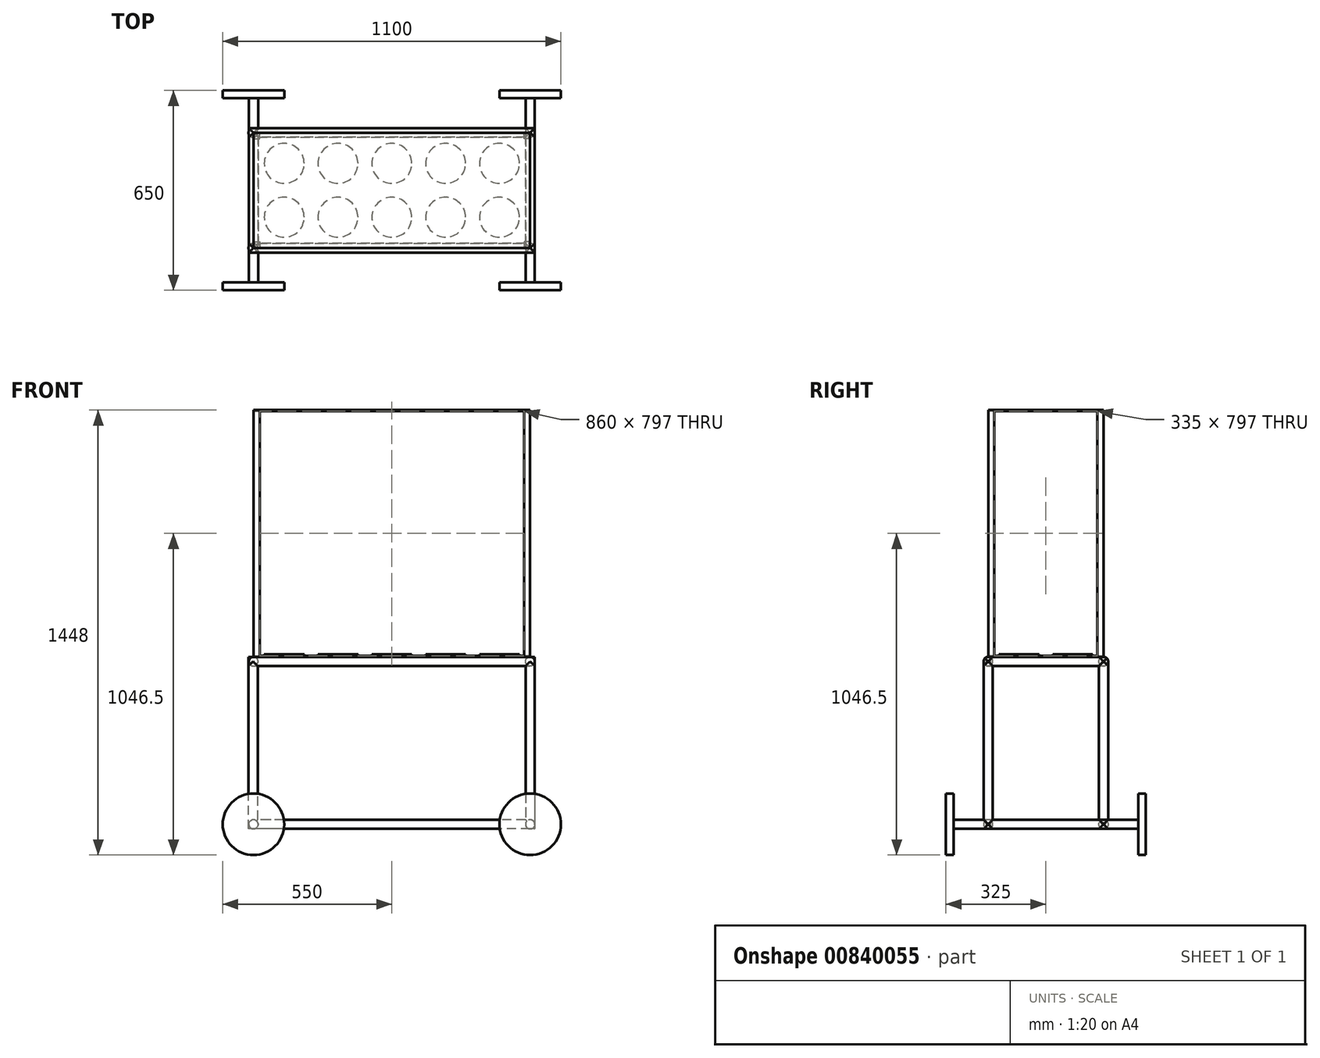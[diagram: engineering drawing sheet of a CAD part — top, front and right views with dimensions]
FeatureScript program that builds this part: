
annotation { "Feature Type Name" : "Feature", "Feature Type Description" : "" }
export const myFeature = defineFeature(function(context is Context, id is Id, definition is map)
    precondition{}
    {
        {
            var Q0;
            Q0=qCreatedBy(makeId("Top.planeOp"),FACE);
            var sketch = newSketch(context, id + "F0", { "sketchPlane" : qUnion([Q0])});
            skLineSegment(sketch, "E0", {"start": v(-450, 0) * mm, "end": v(-450, 187.5) * mm});
            skLineSegment(sketch, "E1", {"start": v(-450, 187.5) * mm, "end": v(0, 187.5) * mm});
            skLineSegment(sketch, "E2.MirrorCS", {"start": v(450, 0) * mm, "end": v(450, 187.5) * mm});
            skLineSegment(sketch, "E3.MirrorCS", {"start": v(450, 187.5) * mm, "end": v(0, 187.5) * mm});
            skLineSegment(sketch, "E4.MirrorCS", {"start": v(-450, 0) * mm, "end": v(-450, -187.5) * mm});
            skLineSegment(sketch, "E5.MirrorCS", {"start": v(-450, -187.5) * mm, "end": v(0, -187.5) * mm});
            skLineSegment(sketch, "E6.MirrorCS", {"start": v(450, -187.5) * mm, "end": v(0, -187.5) * mm});
            skLineSegment(sketch, "E7.MirrorCS", {"start": v(450, 0) * mm, "end": v(450, -187.5) * mm});
            skSolve(sketch);
        }
        {
            var Q0;
            Q0=qCreatedBy(makeId("Right.planeOp"),FACE);
            var sketch = newSketch(context, id + "F1", { "sketchPlane" : qUnion([Q0])});
            skCircle(sketch, "E8", {"center": v(187.5, 0) * mm, "radius": 15 * mm});
            skSolve(sketch);
        }
        {
            var Q0;
            Q0=makeQuery(id+"F0.imprint","IMPRINT",FACE,{"disambiguationData":[TD([[makeQuery(id+"F0.imprint","IMPRINT",EDGE,{"derivedFrom":sQuery(id+"F0.wireOp",EDGE,"E0")}),-1.0]])]});
            cPlane(context, id + "F2", {"entities" : qUnion([Q0]), "cplaneType" : CPlaneType.OFFSET, "offset" : 530 * mm, "width" : 150 * mm, "height" : 150 * mm});
        }
        {
            var Q0;
            Q0=qCreatedBy(id+"F2.planeOp",FACE);
            var sketch = newSketch(context, id + "F3", { "sketchPlane" : qUnion([Q0])});
            skLineSegment(sketch, "E9", {"start": v(-450, -187.5) * mm, "end": v(-450, 187.5) * mm});
            skLineSegment(sketch, "E10", {"start": v(-450, 187.5) * mm, "end": v(450, 187.5) * mm});
            skLineSegment(sketch, "E11", {"start": v(450, 187.5) * mm, "end": v(450, -187.5) * mm});
            skLineSegment(sketch, "E12", {"start": v(450, -187.5) * mm, "end": v(-450, -187.5) * mm});
            skSolve(sketch);
        }
        {
            var Q0;
            Q0=qCreatedBy(makeId("Front.planeOp"),FACE);
            cPlane(context, id + "F4", {"entities" : qUnion([Q0]), "cplaneType" : CPlaneType.OFFSET, "offset" : 187.5 * mm, "width" : 150 * mm, "height" : 150 * mm});
        }
        {
            var Q0;
            Q0=qCreatedBy(id+"F4.planeOp",FACE);
            var sketch = newSketch(context, id + "F5", { "sketchPlane" : qUnion([Q0])});
            skLineSegment(sketch, "E13", {"start": v(-450, 0) * mm, "end": v(-450, 530) * mm});
            skLineSegment(sketch, "E14", {"start": v(-450, 530) * mm, "end": v(450, 530) * mm});
            skLineSegment(sketch, "E15", {"start": v(450, 530) * mm, "end": v(450, 0) * mm});
            skLineSegment(sketch, "E16", {"start": v(450, 0) * mm, "end": v(-450, 0) * mm});
            skSolve(sketch);
        }
        {
            var Q0;
            Q0=qCreatedBy(makeId("Front.planeOp"),FACE);
            cPlane(context, id + "F6", {"entities" : qUnion([Q0]), "cplaneType" : CPlaneType.OFFSET, "offset" : 187.5 * mm, "oppositeDirection" : true, "width" : 150 * mm, "height" : 150 * mm});
        }
        {
            var Q0;
            Q0=qCreatedBy(id+"F6.planeOp",FACE);
            var sketch = newSketch(context, id + "F7", { "sketchPlane" : qUnion([Q0])});
            skLineSegment(sketch, "E17", {"start": v(450, 0) * mm, "end": v(450, 530) * mm});
            skLineSegment(sketch, "E18", {"start": v(450, 530) * mm, "end": v(-451.38, 530) * mm});
            skLineSegment(sketch, "E19", {"start": v(-451.38, 530) * mm, "end": v(-451.38, 0) * mm});
            skLineSegment(sketch, "E20", {"start": v(-451.38, 0) * mm, "end": v(450, 0) * mm});
            skSolve(sketch);
        }
        {
            var Q0;
            Q0=qCreatedBy(makeId("Right.planeOp"),FACE);
            var sketch = newSketch(context, id + "F8", { "sketchPlane" : qUnion([Q0])});
            skCircle(sketch, "E21", {"center": v(-187.5, 530) * mm, "radius": 15 * mm});
            skSolve(sketch);
        }
        {
            var Q0;
            Q0=qCreatedBy(makeId("Right.planeOp"),FACE);
            var sketch = newSketch(context, id + "F9", { "sketchPlane" : qUnion([Q0])});
            skCircle(sketch, "E22", {"center": v(187.5, 530) * mm, "radius": 15 * mm});
            skSolve(sketch);
        }
        {
            var Q0;
            Q0=makeQuery(id+"F9.imprint","IMPRINT",FACE,{"disambiguationData":[TD([[makeQuery(id+"F9.imprint","IMPRINT",EDGE,{"derivedFrom":sQuery(id+"F9.wireOp",EDGE,"E22")}),1.0]])]});
            var Q1;
            Q1=sQuery(id+"F7.wireOp",EDGE,"E18");
            var Q2;
            Q2=sQuery(id+"F7.wireOp",EDGE,"E17");
            var Q3;
            Q3=sQuery(id+"F7.wireOp",EDGE,"E20");
            var Q4;
            Q4=sQuery(id+"F7.wireOp",EDGE,"E19");
            sweep(context, id + "F10", {"profiles" : qUnion([Q0]), "path" : qUnion([Q1, Q2, Q3, Q4])});
        }
        {
            var Q0;
            Q0 = qSketchRegion(id + "F8", true);
            var Q1;
            Q1=sQuery(id+"F3.wireOp",EDGE,"E12");
            var Q2;
            Q2=sQuery(id+"F3.wireOp",EDGE,"E9");
            var Q3;
            Q3=sQuery(id+"F3.wireOp",EDGE,"E10");
            var Q4;
            Q4=sQuery(id+"F3.wireOp",EDGE,"E11");
            sweep(context, id + "F11", {"operationType" : NewBodyOperationType.ADD, "profiles" : qUnion([Q0]), "path" : qUnion([Q1, Q2, Q3, Q4])});
        }
        {
            var Q0;
            Q0=qCreatedBy(id+"F2.planeOp",FACE);
            cPlane(context, id + "F12", {"entities" : qUnion([Q0]), "cplaneType" : CPlaneType.OFFSET, "offset" : 15 * mm, "width" : 150 * mm, "height" : 150 * mm});
        }
        {
            var Q0;
            Q0=qCreatedBy(id+"F12.planeOp",FACE);
            var sketch = newSketch(context, id + "F13", { "sketchPlane" : qUnion([Q0])});
            skLineSegment(sketch, "E23", {"start": v(-450, 0) * mm, "end": v(-450, 187.5) * mm});
            skLineSegment(sketch, "E24", {"start": v(-450, 187.5) * mm, "end": v(450, 187.5) * mm});
            skLineSegment(sketch, "E25", {"start": v(450, 187.5) * mm, "end": v(450, -187.5) * mm});
            skLineSegment(sketch, "E26", {"start": v(450, -187.5) * mm, "end": v(-450, -187.5) * mm});
            skLineSegment(sketch, "E27", {"start": v(-450, -187.5) * mm, "end": v(-450, 0) * mm});
            skSolve(sketch);
        }
        {
            var Q0;
            Q0=makeQuery(id+"F13.imprint","IMPRINT",FACE,{"disambiguationData":[TD([[makeQuery(id+"F13.imprint","IMPRINT",EDGE,{"derivedFrom":sQuery(id+"F13.wireOp",EDGE,"E23")}),-1.0]])]});
            extrude(context, id + "F14", {"entities" : qUnion([Q0]), "depth" : 3 * mm, "offsetDistance" : 25 * mm});
        }
        {
            var Q0;
            Q0=makeQuery(id+"F14.opExtrude","CAP_FACE",FACE,{"disambiguationData":[OSD([sQuery(id+"F13.wireOp",EDGE,"E23"),sQuery(id+"F13.wireOp",EDGE,"E24"),sQuery(id+"F13.wireOp",EDGE,"E25"),sQuery(id+"F13.wireOp",EDGE,"E26"),sQuery(id+"F13.wireOp",EDGE,"E27")])],"isStart":false});
            var sketch = newSketch(context, id + "F15", { "sketchPlane" : qUnion([Q0])});
            skCircle(sketch, "E28", {"center": v(-350, -87.5) * mm, "radius": 65 * mm});
            skCircle(sketch, "E29", {"center": v(-350, 87.5) * mm, "radius": 65 * mm});
            skCircle(sketch, "E30", {"center": v(-175, 87.5) * mm, "radius": 65 * mm});
            skCircle(sketch, "E31", {"center": v(0, 87.5) * mm, "radius": 65 * mm});
            skCircle(sketch, "E32", {"center": v(175, 87.5) * mm, "radius": 65 * mm});
            skCircle(sketch, "E33", {"center": v(350, 87.5) * mm, "radius": 65 * mm});
            skCircle(sketch, "E34", {"center": v(-175, -87.5) * mm, "radius": 65 * mm});
            skCircle(sketch, "E35", {"center": v(0, -87.5) * mm, "radius": 65 * mm});
            skCircle(sketch, "E36", {"center": v(175, -87.5) * mm, "radius": 65 * mm});
            skCircle(sketch, "E37", {"center": v(350, -87.5) * mm, "radius": 65 * mm});
            skSolve(sketch);
        }
        {
            var Q0;
            Q0 = qSketchRegion(id + "F15", true);
            extrude(context, id + "F16", {"entities" : qUnion([Q0]), "operationType" : NewBodyOperationType.ADD, "depth" : 5 * mm, "offsetDistance" : 25 * mm});
        }
        {
            var Q0;
            Q0=qCreatedBy(makeId("Top.planeOp"),FACE);
            var sketch = newSketch(context, id + "F17", { "sketchPlane" : qUnion([Q0])});
            skLineSegment(sketch, "E38", {"start": v(-450, 0) * mm, "end": v(-450, -300) * mm});
            skLineSegment(sketch, "E39", {"start": v(-450, 0) * mm, "end": v(-450, 300) * mm});
            skLineSegment(sketch, "E40", {"start": v(450, 0) * mm, "end": v(450, 300) * mm});
            skLineSegment(sketch, "E41", {"start": v(450, -300) * mm, "end": v(450, 0) * mm});
            skSolve(sketch);
        }
        {
            var Q0;
            Q0=qCreatedBy(makeId("Front.planeOp"),FACE);
            var sketch = newSketch(context, id + "F18", { "sketchPlane" : qUnion([Q0])});
            skLineSegment(sketch, "E42", {"start": v(0, 0) * mm, "end": v(450, 0) * mm, "construction": true});
            skLineSegment(sketch, "E43", {"start": v(450, 0) * mm, "end": v(-450, 0) * mm, "construction": true});
            skCircle(sketch, "E44", {"center": v(450, 0) * mm, "radius": 15 * mm});
            skCircle(sketch, "E45", {"center": v(-450, 0) * mm, "radius": 15 * mm});
            skSolve(sketch);
        }
        {
            var Q0;
            Q0=makeQuery(id+"F18.imprint","IMPRINT",FACE,{"disambiguationData":[TD([[makeQuery(id+"F18.imprint","IMPRINT",EDGE,{"derivedFrom":sQuery(id+"F18.wireOp",EDGE,"E45")}),1.0]])]});
            var Q1;
            Q1=sQuery(id+"F17.wireOp",EDGE,"E38");
            var Q2;
            Q2=sQuery(id+"F17.wireOp",EDGE,"E39");
            sweep(context, id + "F19", {"operationType" : NewBodyOperationType.ADD, "profiles" : qUnion([Q0]), "path" : qUnion([Q1, Q2])});
        }
        {
            var Q0;
            Q0 = qSketchRegion(id + "F18", true);
            var Q1;
            Q1=sQuery(id+"F17.wireOp",EDGE,"E41");
            var Q2;
            Q2=sQuery(id+"F17.wireOp",EDGE,"E40");
            sweep(context, id + "F20", {"operationType" : NewBodyOperationType.ADD, "profiles" : qUnion([Q0]), "path" : qUnion([Q1, Q2])});
        }
        {
            var Q0;
            Q0=qCreatedBy(makeId("Front.planeOp"),FACE);
            cPlane(context, id + "F21", {"entities" : qUnion([Q0]), "cplaneType" : CPlaneType.OFFSET, "offset" : 300 * mm, "width" : 150 * mm, "height" : 150 * mm});
        }
        {
            var Q0;
            Q0=qCreatedBy(id+"F21.planeOp",FACE);
            var sketch = newSketch(context, id + "F22", { "sketchPlane" : qUnion([Q0])});
            skCircle(sketch, "E46", {"center": v(-450, 0) * mm, "radius": 100 * mm});
            skCircle(sketch, "E47", {"center": v(450, 0) * mm, "radius": 100 * mm});
            skSolve(sketch);
        }
        {
            var Q0;
            Q0=makeQuery(id+"F22.imprint","IMPRINT",FACE,{"disambiguationData":[TD([[makeQuery(id+"F22.imprint","IMPRINT",EDGE,{"derivedFrom":sQuery(id+"F22.wireOp",EDGE,"E46")}),1.0]])]});
            var Q1;
            Q1=makeQuery(id+"F22.imprint","IMPRINT",FACE,{"disambiguationData":[TD([[makeQuery(id+"F22.imprint","IMPRINT",EDGE,{"derivedFrom":sQuery(id+"F22.wireOp",EDGE,"E47")}),1.0]])]});
            extrude(context, id + "F23", {"entities" : qUnion([Q0, Q1]), "operationType" : NewBodyOperationType.ADD, "depth" : 25 * mm, "offsetDistance" : 25 * mm});
        }
        {
            var Q0;
            Q0=makeQuery(id+"F10.opSweep","SWEPT_BODY",BODY,{"disambiguationData":[OSD([sQuery(id+"F7.wireOp",EDGE,"E17"),sQuery(id+"F9.wireOp",EDGE,"E22")])]});
            var Q1;
            Q1=qCreatedBy(makeId("Front.planeOp"),FACE);
            mirror(context, id + "F24", {"entities" : qUnion([Q0]), "mirrorPlane" : qUnion([Q1])});
        }
        {
            var Q0;
            Q0=makeQuery(id+"F14.opExtrude","CAP_FACE",FACE,{"disambiguationData":[OSD([sQuery(id+"F13.wireOp",EDGE,"E23"),sQuery(id+"F13.wireOp",EDGE,"E24"),sQuery(id+"F13.wireOp",EDGE,"E25"),sQuery(id+"F13.wireOp",EDGE,"E26"),sQuery(id+"F13.wireOp",EDGE,"E27")])],"isStart":false});
            var sketch = newSketch(context, id + "F25", { "sketchPlane" : qUnion([Q0])});
            skLineSegment(sketch, "E48", {"start": v(0, 187.5) * mm, "end": v(-450, 187.5) * mm, "construction": true});
            skLineSegment(sketch, "E49", {"start": v(-450, 187.5) * mm, "end": v(-450, -187.5) * mm, "construction": true});
            skLineSegment(sketch, "E50", {"start": v(-450, -187.5) * mm, "end": v(450, -187.5) * mm, "construction": true});
            skLineSegment(sketch, "E51", {"start": v(450, -187.5) * mm, "end": v(450, 187.5) * mm, "construction": true});
            skLineSegment(sketch, "E52", {"start": v(450, 187.5) * mm, "end": v(0, 187.5) * mm, "construction": true});
            skLineSegment(sketch, "E53", {"start": v(-450, 187.5) * mm, "end": v(-450, 167.5) * mm});
            skLineSegment(sketch, "E54", {"start": v(-450, 167.5) * mm, "end": v(-430, 167.5) * mm});
            skLineSegment(sketch, "E55", {"start": v(-430, 167.5) * mm, "end": v(-430, 187.5) * mm});
            skLineSegment(sketch, "E56", {"start": v(-430, 187.5) * mm, "end": v(-450, 187.5) * mm});
            skLineSegment(sketch, "E57", {"start": v(0, 0) * mm, "end": v(0, 187.5) * mm, "construction": true});
            skLineSegment(sketch, "E58.MirrorCS", {"start": v(430, 167.5) * mm, "end": v(430, 187.5) * mm});
            skLineSegment(sketch, "E59.MirrorCS", {"start": v(450, 167.5) * mm, "end": v(430, 167.5) * mm});
            skLineSegment(sketch, "E60.MirrorCS", {"start": v(450, 187.5) * mm, "end": v(450, -187.5) * mm, "construction": true});
            skLineSegment(sketch, "E61.MirrorCS", {"start": v(0, 187.5) * mm, "end": v(450, 187.5) * mm, "construction": true});
            skLineSegment(sketch, "E62", {"start": v(430, 187.5) * mm, "end": v(450, 187.5) * mm, "construction": true});
            skLineSegment(sketch, "E63", {"start": v(450, 167.5) * mm, "end": v(450, 187.5) * mm});
            skLineSegment(sketch, "E64", {"start": v(430, 187.5) * mm, "end": v(450, 187.5) * mm});
            skLineSegment(sketch, "E65.MirrorCS", {"start": v(450, -167.5) * mm, "end": v(430, -167.5) * mm});
            skLineSegment(sketch, "E66.MirrorCS", {"start": v(430, -167.5) * mm, "end": v(430, -187.5) * mm});
            skLineSegment(sketch, "E67", {"start": v(430, -187.5) * mm, "end": v(450, -187.5) * mm});
            skLineSegment(sketch, "E68.MirrorCS", {"start": v(-450, -167.5) * mm, "end": v(-430, -167.5) * mm});
            skLineSegment(sketch, "E69.MirrorCS", {"start": v(-430, -167.5) * mm, "end": v(-430, -187.5) * mm});
            skLineSegment(sketch, "E70", {"start": v(-430, -187.5) * mm, "end": v(-450, -187.5) * mm});
            skLineSegment(sketch, "E71", {"start": v(-450, -167.5) * mm, "end": v(-450, -187.5) * mm});
            skSolve(sketch);
        }
        {
            var Q0;
            Q0=makeQuery(id+"F25.imprint","IMPRINT",FACE,{"disambiguationData":[TD([[makeQuery(id+"F25.imprint","IMPRINT",EDGE,{"derivedFrom":sQuery(id+"F25.wireOp",EDGE,"E68.MirrorCS")}),-1.0]])]});
            var Q1;
            Q1=makeQuery(id+"F25.imprint","IMPRINT",FACE,{"disambiguationData":[TD([[makeQuery(id+"F25.imprint","IMPRINT",EDGE,{"derivedFrom":sQuery(id+"F25.wireOp",EDGE,"E53")}),-1.0]])]});
            var Q2;
            Q2=makeQuery(id+"F25.imprint","IMPRINT",FACE,{"disambiguationData":[TD([[makeQuery(id+"F25.imprint","IMPRINT",EDGE,{"derivedFrom":sQuery(id+"F25.wireOp",EDGE,"E58.MirrorCS")}),-1.0]])]});
            var Q3;
            {var subQ0=sQuery(id+"F25.wireOp",EDGE,"E65.MirrorCS");Q3=makeQuery(id+"F25.imprint","IMPRINT",FACE,{"disambiguationData":[TD([[makeQuery(id+"F25.imprint","IMPRINT",EDGE,{"derivedFrom":subQ0}),1.0]])]});}
            extrude(context, id + "F26", {"entities" : qUnion([Q0, Q1, Q2, Q3]), "operationType" : NewBodyOperationType.ADD, "depth" : 800 * mm, "offsetDistance" : 25 * mm});
        }
        {
            var Q0;
            Q0=makeQuery(id+"F26.opExtrude","CAP_FACE",FACE,{"disambiguationData":[OSD([sQuery(id+"F25.wireOp",EDGE,"E53"),sQuery(id+"F25.wireOp",EDGE,"E54"),sQuery(id+"F25.wireOp",EDGE,"E55"),sQuery(id+"F25.wireOp",EDGE,"E56")])],"isStart":false});
            var sketch = newSketch(context, id + "F27", { "sketchPlane" : qUnion([Q0])});
            skLineSegment(sketch, "E72", {"start": v(0, 0) * mm, "end": v(0, 187.5) * mm, "construction": true});
            skLineSegment(sketch, "E73", {"start": v(0, 187.5) * mm, "end": v(-450, 187.5) * mm, "construction": true});
            skLineSegment(sketch, "E74.bottom", {"start": v(-450, 187.5) * mm, "end": v(450, 187.5) * mm});
            skLineSegment(sketch, "E74.top", {"start": v(-450, -187.5) * mm, "end": v(450, -187.5) * mm});
            skLineSegment(sketch, "E74.left", {"start": v(-450, 187.5) * mm, "end": v(-450, -187.5) * mm});
            skLineSegment(sketch, "E74.right", {"start": v(450, 187.5) * mm, "end": v(450, -187.5) * mm});
            skSolve(sketch);
        }
        {
            var Q0;
            {var subQ3=sQuery(id+"F27.wireOp",EDGE,"E74.top");Q0=makeQuery(id+"F27.imprint","IMPRINT",FACE,{"disambiguationData":[TD([[makeQuery(id+"F27.imprint","IMPRINT",EDGE,{"derivedFrom":subQ3}),1.0]])]});}
            extrude(context, id + "F28", {"entities" : qUnion([Q0]), "operationType" : NewBodyOperationType.ADD, "oppositeDirection" : true, "depth" : 3 * mm, "offsetDistance" : 25 * mm});
        }
    });
